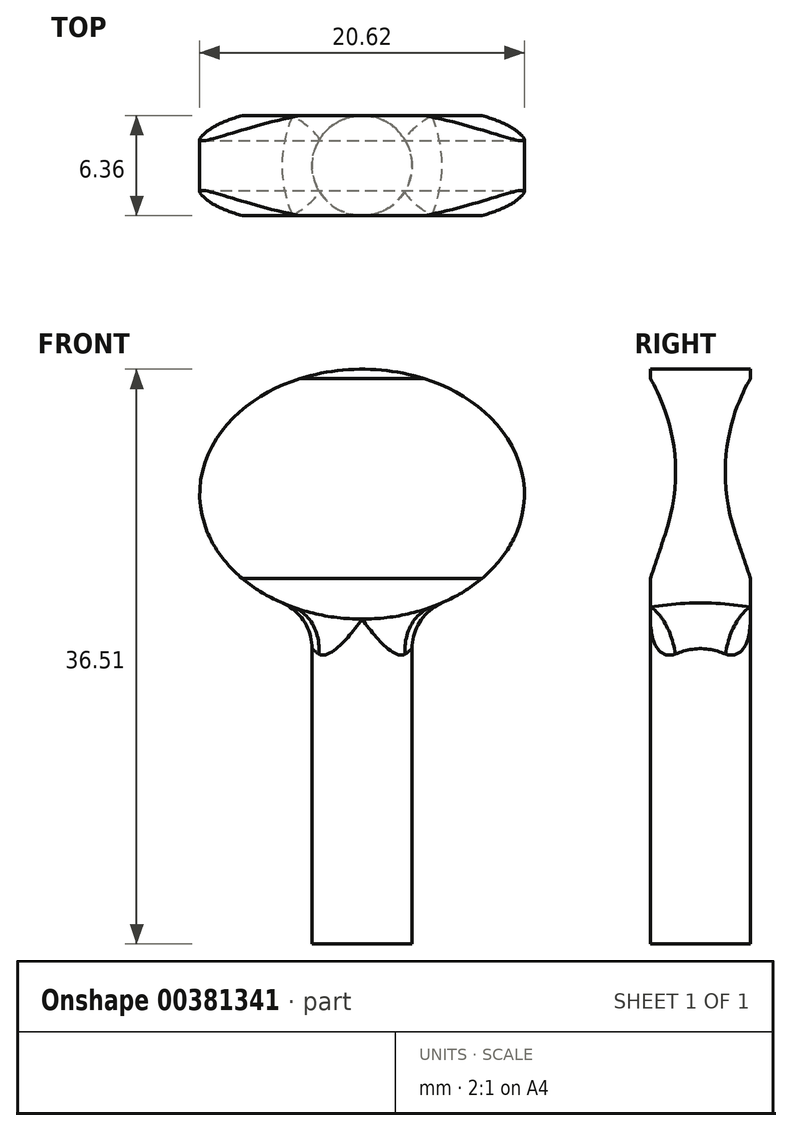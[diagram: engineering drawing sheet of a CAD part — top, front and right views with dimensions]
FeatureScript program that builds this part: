
annotation { "Feature Type Name" : "Feature", "Feature Type Description" : "" }
export const myFeature = defineFeature(function(context is Context, id is Id, definition is map)
    precondition{}
    {
        {
            var Q0;
            Q0=qCreatedBy(makeId("Top.planeOp"),FACE);
            var sketch = newSketch(context, id + "F0", { "sketchPlane" : qUnion([Q0])});
            skCircle(sketch, "E0", {"center": v(0, 0) * mm, "radius": 3.18 * mm});
            skSolve(sketch);
        }
        {
            var Q0;
            Q0=qCreatedBy(makeId("Right.planeOp"),FACE);
            var sketch = newSketch(context, id + "F1", { "sketchPlane" : qUnion([Q0])});
            skLineSegment(sketch, "E1", {"start": v(0, -63.5) * mm, "end": v(0, 63.5) * mm});
            skSolve(sketch);
        }
        {
            var Q0;
            Q0=qSketchRegion(id+"F0",true);
            extrude(context, id + "F2", {"entities" : qUnion([Q0]), "depth" : 25.4 * mm});
        }
        {
            var Q0;
            Q0=qCreatedBy(makeId("Front.planeOp"),FACE);
            var sketch = newSketch(context, id + "F3", { "sketchPlane" : qUnion([Q0])});
            skEllipse(sketch, "E2", {"center": v(0, 28.58) * mm, "majorRadius": 10.31 * mm, "minorRadius": 7.94 * mm, "majorAxis": v(1, 0)});
            skSolve(sketch);
        }
        {
            var Q0;
            Q0=makeQuery(id+"F3.imprint","IMPRINT",FACE,{"disambiguationData":[TD([[makeQuery(id+"F3.imprint","IMPRINT",EDGE,{"derivedFrom":sQuery(id+"F3.wireOp",EDGE,"E2")}),1.0]])]});
            extrude(context, id + "F4", {"entities" : qUnion([Q0]), "operationType" : NewBodyOperationType.ADD, "endBound" : BoundingType.SYMMETRIC, "depth" : 6.35 * mm});
        }
        {
            var Q0;
            Q0=makeQuery(id+"F4.boolean.opBoolean","INTERSECT",EDGE,{"disambiguationData":[OD(1.0)],"derivedFrom":[makeQuery(id+"F2.opExtrude","SWEPT_FACE",FACE,{"disambiguationData":[OSD([sQuery(id+"F0.wireOp",EDGE,"E0")])]}),makeQuery(id+"F4.opExtrude","SWEPT_FACE",FACE,{"disambiguationData":[OSD([sQuery(id+"F3.wireOp",EDGE,"E2")])]})]});
            fillet(context, id + "F5", {"entities" : qUnion([Q0]), "radius" : 3.17 * mm, "tangentPropagation" : true, "allowEdgeOverflow" : false});
        }
        {
            var Q0;
            Q0=qCreatedBy(makeId("Right.planeOp"),FACE);
            var sketch = newSketch(context, id + "F6", { "sketchPlane" : qUnion([Q0])});
            skArc(sketch, "E3", {"start": v(6.02, 39.23) * mm, "mid": v(2.06, 33.3) * mm, "end": v(2.19, 26.18) * mm});
            skLineSegment(sketch, "E4", {"start": v(2.19, 26.18) * mm, "end": v(5.25, 17) * mm});
            skLineSegment(sketch, "E5", {"start": v(5.25, 17) * mm, "end": v(10.18, 17) * mm});
            skLineSegment(sketch, "E6", {"start": v(6.02, 39.23) * mm, "end": v(6.02, 17) * mm});
            skArc(sketch, "E7.MirrorCS", {"start": v(-6.02, 39.23) * mm, "mid": v(-2.06, 33.3) * mm, "end": v(-2.19, 26.18) * mm});
            skLineSegment(sketch, "E8.MirrorCS", {"start": v(-2.19, 26.18) * mm, "end": v(-5.25, 17) * mm});
            skLineSegment(sketch, "E9.MirrorCS", {"start": v(-6.02, 39.23) * mm, "end": v(-6.02, 17) * mm});
            skLineSegment(sketch, "E10.MirrorCS", {"start": v(-5.25, 17) * mm, "end": v(-10.18, 17) * mm});
            skSolve(sketch);
        }
        {
            var Q0;
            Q0=qSketchRegion(id+"F6",true);
            extrude(context, id + "F7", {"entities" : qUnion([Q0]), "operationType" : NewBodyOperationType.REMOVE, "endBound" : BoundingType.SYMMETRIC, "oppositeDirection" : true, "depth" : 50.8 * mm});
        }
    });
